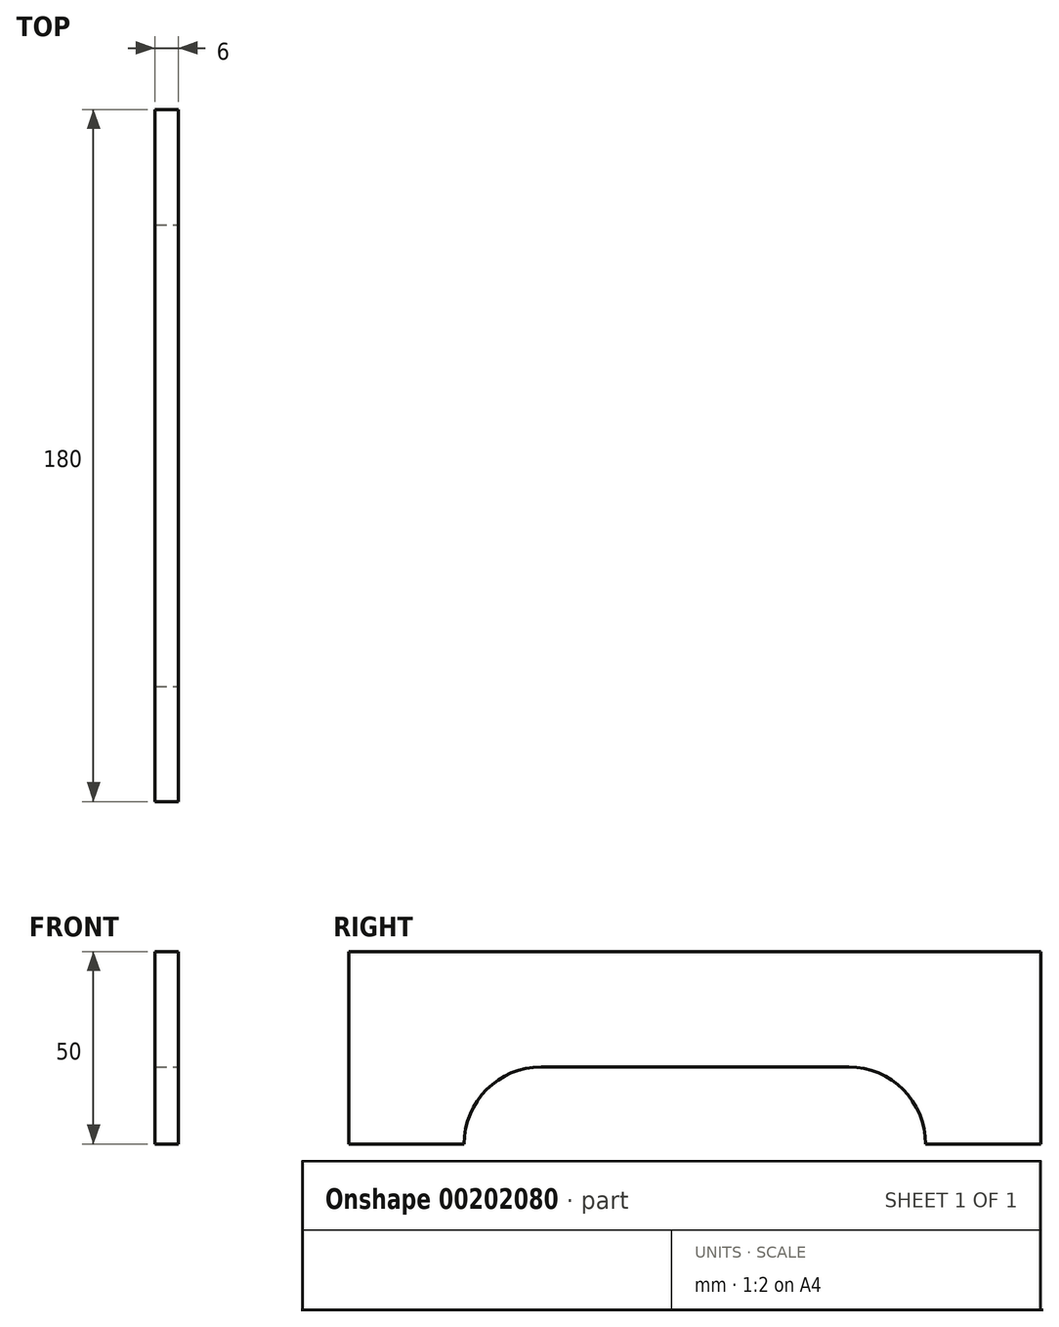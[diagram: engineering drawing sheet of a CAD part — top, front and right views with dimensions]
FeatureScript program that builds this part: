
annotation { "Feature Type Name" : "Feature", "Feature Type Description" : "" }
export const myFeature = defineFeature(function(context is Context, id is Id, definition is map)
    precondition{}
    {
        {
            var Q0;
            Q0=qCreatedBy(makeId("Right.planeOp"),FACE);
            var sketch = newSketch(context, id + "F0", { "sketchPlane" : qUnion([Q0])});
            skLineSegment(sketch, "E0.bottom", {"start": v(-90, -25) * mm, "end": v(90, -25) * mm});
            skLineSegment(sketch, "E0.top", {"start": v(-90, 25) * mm, "end": v(90, 25) * mm});
            skLineSegment(sketch, "E0.left", {"start": v(-90, -25) * mm, "end": v(-90, 25) * mm});
            skLineSegment(sketch, "E0.right", {"start": v(90, -25) * mm, "end": v(90, 25) * mm});
            skPoint(sketch, "E0.middle", {"position": v(0, 0) * mm});
            skSolve(sketch);
        }
        {
            var Q0;
            Q0 = qSketchRegion(id + "F0", true);
            extrude(context, id + "F1", {"entities" : qUnion([Q0]), "depth" : 6 * mm});
        }
        {
            var Q0;
            Q0=makeQuery(id+"F1.opExtrude","CAP_FACE",FACE,{"disambiguationData":[OSD([sQuery(id+"F0.wireOp",EDGE,"E0.bottom"),sQuery(id+"F0.wireOp",EDGE,"E0.top"),sQuery(id+"F0.wireOp",EDGE,"E0.left"),sQuery(id+"F0.wireOp",EDGE,"E0.right")])],"isStart":false});
            var sketch = newSketch(context, id + "F2", { "sketchPlane" : qUnion([Q0])});
            skLineSegment(sketch, "E1.bottom", {"start": v(-60, -25) * mm, "end": v(60, -25) * mm});
            skLineSegment(sketch, "E1.top", {"start": v(-60, -5) * mm, "end": v(60, -5) * mm});
            skLineSegment(sketch, "E1.left", {"start": v(-60, -25) * mm, "end": v(-60, -5) * mm});
            skLineSegment(sketch, "E1.right", {"start": v(60, -25) * mm, "end": v(60, -5) * mm});
            skSolve(sketch);
        }
        {
            var Q0;
            Q0=makeQuery(id+"F2.imprint","IMPRINT",FACE,{"disambiguationData":[TD([[makeQuery(id+"F2.imprint","IMPRINT",EDGE,{"derivedFrom":sQuery(id+"F2.wireOp",EDGE,"E1.bottom")}),1.0]])]});
            extrude(context, id + "F3", {"entities" : qUnion([Q0]), "operationType" : NewBodyOperationType.REMOVE, "oppositeDirection" : true, "depth" : 25 * mm});
        }
        {
            var Q0;
            Q0=makeQuery(id+"F3.boolean.opBoolean","COPY",EDGE,{"derivedFrom":makeQuery(id+"F3.opExtrude","SWEPT_EDGE",EDGE,{"disambiguationData":[OSD([sQuery(id+"F2.wireOp",EDGE,"E1.top"),sQuery(id+"F2.wireOp",EDGE,"E1.right")])]})});
            var Q1;
            Q1=makeQuery(id+"F3.boolean.opBoolean","COPY",EDGE,{"derivedFrom":makeQuery(id+"F3.opExtrude","SWEPT_EDGE",EDGE,{"disambiguationData":[OSD([sQuery(id+"F2.wireOp",EDGE,"E1.top"),sQuery(id+"F2.wireOp",EDGE,"E1.left")])]})});
            fillet(context, id + "F4", {"entities" : qUnion([Q0, Q1]), "radius" : 20 * mm, "tangentPropagation" : true, "allowEdgeOverflow" : false});
        }
    });
